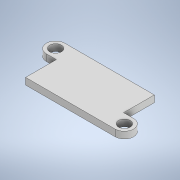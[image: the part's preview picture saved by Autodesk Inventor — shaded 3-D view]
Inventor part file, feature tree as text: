
AUTODESK INVENTOR PART (.ipt)
format: ipt  version: 2020 (Build 240168000, 168)  size: 116,224 bytes
history: native  units: in
note: dims shown in document units (in); Inventor stores cm internally (conversion verified against a paired STEP export)
features: extrude x1, sketch x1
ambient origin geometry x8: Origin, YZ Plane, XZ Plane, XY Plane, X Axis, Y Axis, Z Axis, Center Point
bodies: Solid1 (feature_tree)
feature tree (2):
  extrude  "Extrusion1"  Depth=0.0787in
  sketch  "Sketch1"  dims[d0=0.857in d1=0.5in d2=0.1378in d3=0.1378in d4=0.1575in d5=0.1575in d6=0.2165in d7=0.2165in d8=0.0787in d9=0.0in]
